# Revit family: QUADRATE NEON FLEX RGBW 1312_NDFXRGBW
name_source: partatom
category: Luminarias
units: mm (PartAtom-declared; Revit-internal decimal feet)

## family parameters
Compartido = No
Corte con vacíos al cargar = No
Cota de conector redondo = Diámetro de uso
Origen de luz = Sí
Punto de cálculo de habitación = No
Se basa en plano de trabajo = Sí
Siempre vertical = No
Tipo de pieza = Normal

## types (1)
- QUADRATE NEON FLEX RGBW_NDFXRGBW
    Archivo de red fotométrica = NFXRGBW_QUADRATE NEON FLEX RGBW 1312.IES
    Cambio de temperatura de color de luz atenuada = <Ninguno>
    Comentarios de vataje = 24
    Descripción = TIRA QUADRATE NEON FLEX RGBW 1312 DE PLASTICO FLEXIBLE CON UNA POTENCIA DE 16.5W/M DE UN TIPO DE LED 2835 SMD, USO PARA EXTERIORES IP67, IK08, TECNOLOGIA EN RGBW 2700-3500K, RGB 4500-5000K, PRESENTACION DE 5M, CORTE 6.5CM, AMPERAJE 0.6A, ALIMENTADO A 24V, REQUIERE ACCESORIOS.
    Elevación por defecto = 0 mm  [stored 0 ft]
    Fabricante = BRILLANT
    Filtro de color = 16777215
    Longitud de línea de emisión = 600 mm
    Marca = BRILLANT
    Modelo = NDFXRGBW
    Modelo Lampara = 2835 SMD
    Ángulo de inclinación = 60.00°

note: [stored X ft] marks values corroborated as IEEE doubles in the binary element streams (Revit-internal decimal feet)

## geometry (parser evidence)
native form markers: Blend x2
no freeform markers — native parametric forms only
